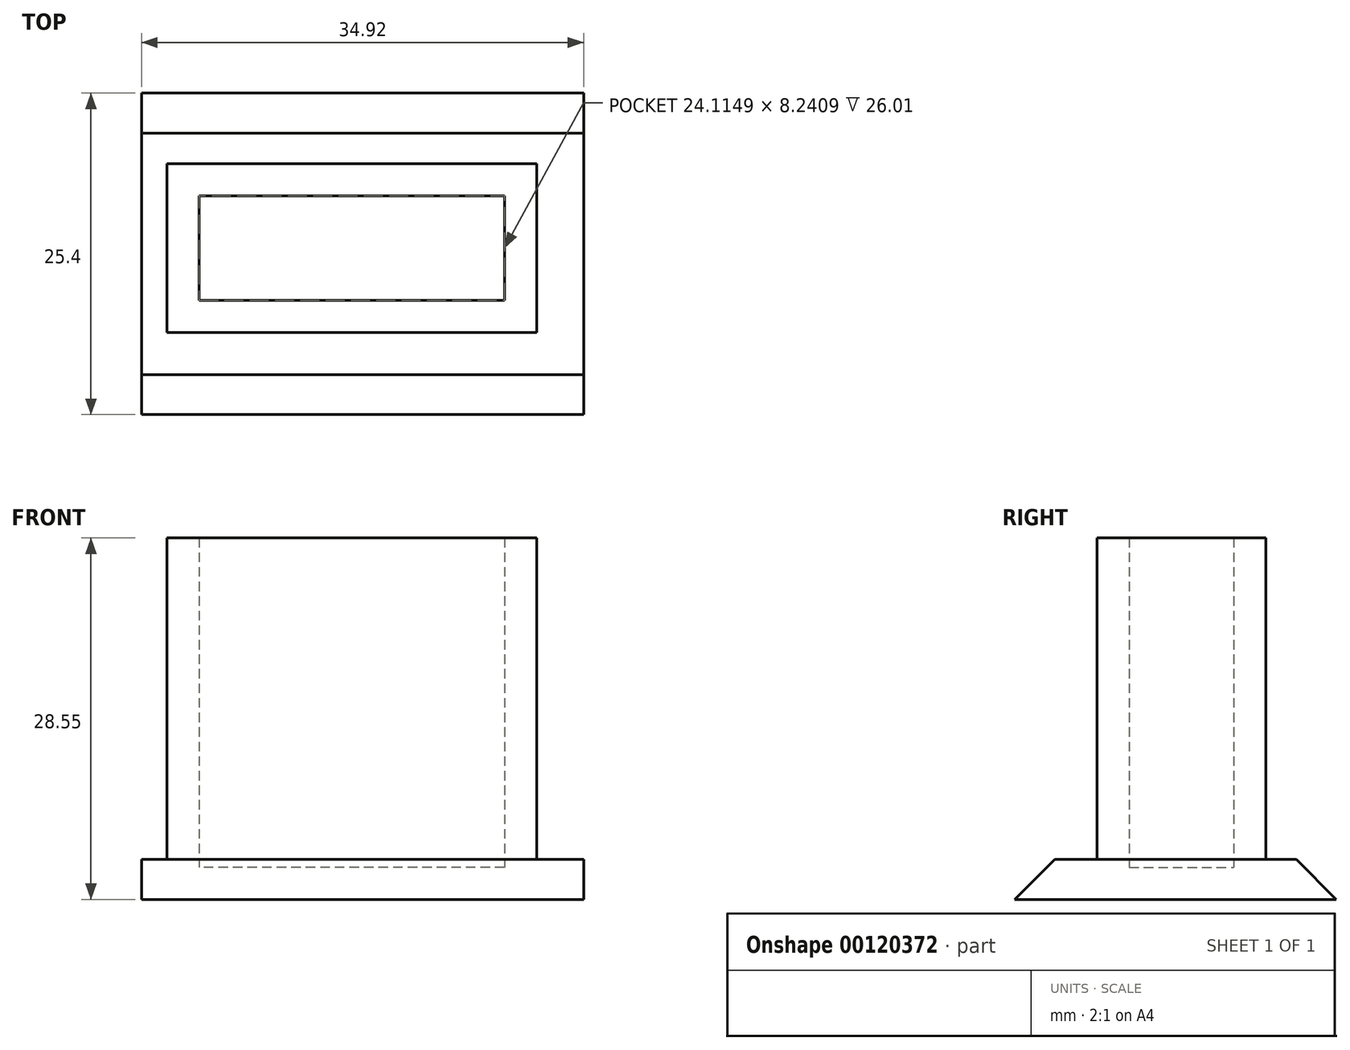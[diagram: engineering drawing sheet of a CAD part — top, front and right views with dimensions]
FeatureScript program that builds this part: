
annotation { "Feature Type Name" : "Feature", "Feature Type Description" : "" }
export const myFeature = defineFeature(function(context is Context, id is Id, definition is map)
    precondition{}
    {
        {
            var Q0;
            Q0=qCreatedBy(makeId("Top.planeOp"),FACE);
            var sketch = newSketch(context, id + "F0", { "sketchPlane" : qUnion([Q0])});
            skLineSegment(sketch, "E0.bottom", {"start": v(-7.71, -7.13) * mm, "end": v(27.21, -7.13) * mm});
            skLineSegment(sketch, "E0.top", {"start": v(-7.71, -32.53) * mm, "end": v(27.21, -32.53) * mm});
            skLineSegment(sketch, "E0.left", {"start": v(-7.71, -7.13) * mm, "end": v(-7.71, -32.53) * mm});
            skLineSegment(sketch, "E0.right", {"start": v(27.21, -7.13) * mm, "end": v(27.21, -32.53) * mm});
            skSolve(sketch);
        }
        {
            var Q0;
            Q0 = qSketchRegion(id + "F0", true);
            extrude(context, id + "F1", {"entities" : qUnion([Q0]), "depth" : 3.15 * mm});
        }
        {
            var Q0;
            Q0=makeQuery(id+"F1.opExtrude","CAP_EDGE",EDGE,{"disambiguationData":[OSD([sQuery(id+"F0.wireOp",EDGE,"E0.top")])],"isStart":false});
            var Q1;
            Q1=makeQuery(id+"F1.opExtrude","CAP_EDGE",EDGE,{"disambiguationData":[OSD([sQuery(id+"F0.wireOp",EDGE,"E0.bottom")])],"isStart":false});
            chamfer(context, id + "F2", {"entities" : qUnion([Q0, Q1]), "width" : 3.15 * mm, "tangentPropagation" : true});
        }
        {
            var Q0;
            Q0=makeQuery(id+"F1.opExtrude","CAP_FACE",FACE,{"disambiguationData":[OSD([sQuery(id+"F0.wireOp",EDGE,"E0.bottom"),sQuery(id+"F0.wireOp",EDGE,"E0.top"),sQuery(id+"F0.wireOp",EDGE,"E0.left"),sQuery(id+"F0.wireOp",EDGE,"E0.right")])],"isStart":false});
            var sketch = newSketch(context, id + "F3", { "sketchPlane" : qUnion([Q0])});
            skLineSegment(sketch, "E1.bottom", {"start": v(-5.7, -12.71) * mm, "end": v(23.5, -12.71) * mm});
            skLineSegment(sketch, "E1.top", {"start": v(-5.7, -26.03) * mm, "end": v(23.5, -26.03) * mm});
            skLineSegment(sketch, "E1.left", {"start": v(-5.7, -12.71) * mm, "end": v(-5.7, -26.03) * mm});
            skLineSegment(sketch, "E1.right", {"start": v(23.5, -12.71) * mm, "end": v(23.5, -26.03) * mm});
            skSolve(sketch);
        }
        {
            var Q0;
            Q0=makeQuery(id+"F3.imprint","IMPRINT",FACE,{"disambiguationData":[TD([[makeQuery(id+"F3.imprint","IMPRINT",EDGE,{"derivedFrom":sQuery(id+"F3.wireOp",EDGE,"E1.bottom")}),-1.0]])]});
            extrude(context, id + "F4", {"entities" : qUnion([Q0]), "operationType" : NewBodyOperationType.ADD, "depth" : 25.4 * mm});
        }
        {
            var Q0;
            Q0=makeQuery(id+"F4.opExtrude","CAP_FACE",FACE,{"disambiguationData":[OSD([sQuery(id+"F3.wireOp",EDGE,"E1.bottom"),sQuery(id+"F3.wireOp",EDGE,"E1.top"),sQuery(id+"F3.wireOp",EDGE,"E1.left"),sQuery(id+"F3.wireOp",EDGE,"E1.right")])],"isStart":false});
            shell(context, id + "F5", {"entities" : qUnion([Q0]), "thickness" : 2.54 * mm});
        }
    });
